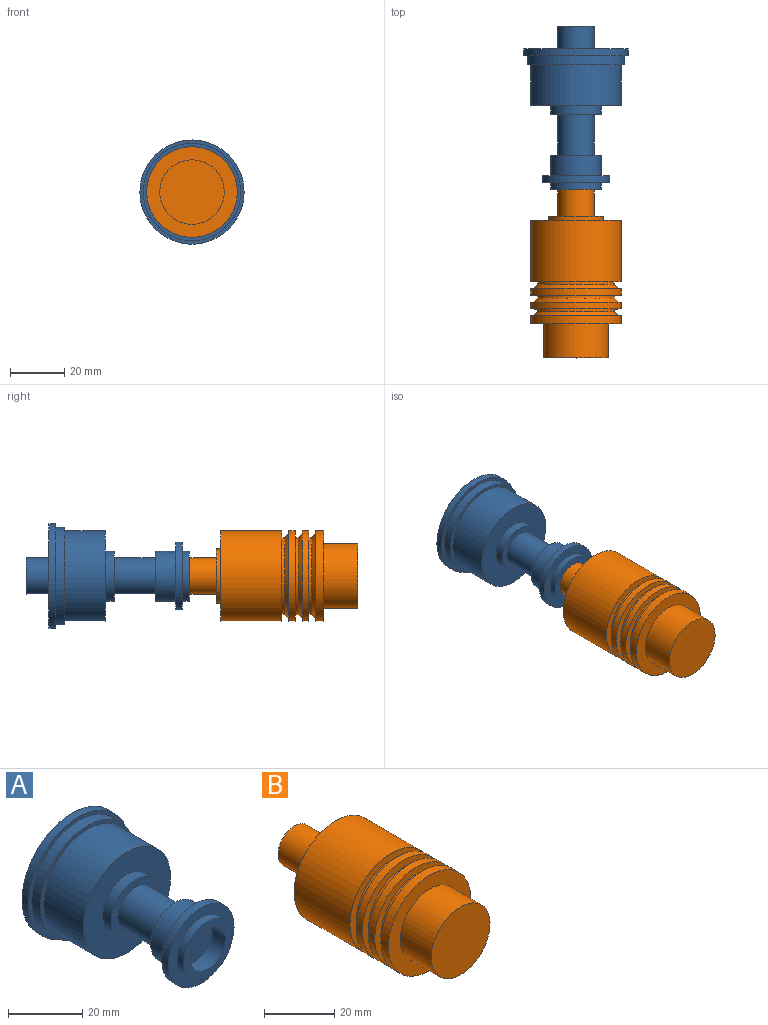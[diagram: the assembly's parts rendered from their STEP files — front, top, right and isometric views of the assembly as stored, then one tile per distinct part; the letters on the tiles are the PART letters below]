
ASSEMBLY  parts=2 mates=1
PART A: 25 faces, bbox 38.3x60x38.3 mm
  f0: plane 18.4x18.4mm, normal (0,-1,0), area 127mm2, adj f20,f21
  f1: plane 13.4x13.4mm, normal (0,1,0), area 71.6mm2, adj f2,f24
  f2: cylinder r=6.7mm len=13.4mm, axis (0,1,0), area 564.1mm2, adj f1,f3
  f3: plane 18.4x18.4mm, normal (0,1,0), area 124.9mm2, adj f2,f4
  f4: cylinder r=9.2mm len=18.4mm, axis (0,1,0), area 289mm2, adj f3,f5
  f5: plane 38.3x38.3mm, normal (0,1,0), area 886.2mm2, adj f4,f6
  f6: cylinder r=19.15mm len=38.3mm, axis (0,1,0), area 300.8mm2, adj f5,f7
  f7: plane 38.3x38.3mm, normal (0,-1,0), area 145.5mm2, adj f6,f8
  f8: cylinder r=17.9mm len=35.8mm, axis (0,1,0), area 371.1mm2, adj f7,f9
  f9: plane 35.8x35.8mm, normal (0,-1,0), area 135.7mm2, adj f8,f10
  f10: cylinder r=16.65mm len=33.3mm, axis (0,1,0), area 1569.2mm2, adj f9,f11
  f11: plane 33.3x33.3mm, normal (0,-1,0), area 605mm2, adj f10,f12
  f12: cylinder r=9.2mm len=18.4mm, axis (0,1,0), area 190.8mm2, adj f11,f13
  f13: plane 18.4x18.4mm, normal (0,-1,0), area 124.9mm2, adj f12,f14
  f14: cylinder r=6.7mm len=15mm, axis (0,1,0), area 631.5mm2, adj f13,f15
  f15: plane 18.4x18.4mm, normal (0,1,0), area 124.9mm2, adj f14,f16
  f16: cylinder r=9.2mm len=18.4mm, axis (0,1,0), area 433.5mm2, adj f15,f17
  f17: plane 25x25mm, normal (0,1,0), area 225mm2, adj f16,f18
  f18: cylinder r=12.5mm len=25mm, axis (0,1,0), area 196.3mm2, adj f17,f19
  f19: plane 25x25mm, normal (0,-1,0), area 225mm2, adj f18,f20
  f20: cylinder r=9.2mm len=18.4mm, axis (0,1,0), area 144.5mm2, adj f0,f19
  f21: cylinder r=6.65mm len=13.3mm, axis (0,-1,0), area 208.9mm2, adj f0,f22
  f22: plane 13.3x13.3mm, normal (0,-1,0), area 138.9mm2, adj f21
  f23: plane 9.4x9.4mm, normal (0,1,0), area 69.4mm2, adj f24
  f24: cylinder r=4.7mm len=10.9mm, axis (0,1,0), area 321.9mm2, adj f1,f23
PART B: 24 faces, bbox 33.3x67x33.3 mm
  f0: plane 33.3x33.3mm, normal (0,-1,0), area 429.8mm2, adj f14,f18
  f1: plane 33.3x33.3mm, normal (0,1,0), area 559.9mm2, adj f2,f20
  f2: cylinder r=16.65mm len=33.3mm, axis (0,1,0), area 2353.8mm2, adj f1,f3
  f3: plane 33.3x33.3mm, normal (0,-1,0), area 241.9mm2, adj f2,f4
  f4: cylinder r=14.15mm len=28.3mm, axis (0,1,0), area 88.9mm2, adj f3,f15
  f5: plane 33.3x33.3mm, normal (0,1,0), area 101.5mm2, adj f6,f15
  f6: cylinder r=16.65mm len=33.3mm, axis (0,1,0), area 261.5mm2, adj f5,f7
  f7: plane 33.3x33.3mm, normal (0,-1,0), area 241.9mm2, adj f6,f8
  f8: cylinder r=14.15mm len=28.3mm, axis (0,1,0), area 88.9mm2, adj f7,f16
  f9: plane 33.3x33.3mm, normal (0,1,0), area 101.5mm2, adj f10,f16
  f10: cylinder r=16.65mm len=33.3mm, axis (0,1,0), area 261.5mm2, adj f9,f11
  f11: plane 33.3x33.3mm, normal (0,-1,0), area 241.9mm2, adj f10,f12
  f12: cylinder r=14.15mm len=28.3mm, axis (0,1,0), area 88.9mm2, adj f11,f17
  f13: plane 33.3x33.3mm, normal (0,1,0), area 101.5mm2, adj f14,f17
  f14: cylinder r=16.65mm len=33.3mm, axis (0,1,0), area 313.8mm2, adj f0,f13
  f15: cone r=14.15mm half-angle=45deg, axis (0,-1,0), area 198.6mm2, adj f4,f5
  f16: cone r=14.15mm half-angle=45deg, axis (0,-1,0), area 198.6mm2, adj f8,f9
  f17: cone r=14.15mm half-angle=45deg, axis (0,-1,0), area 198.6mm2, adj f12,f13
  f18: cylinder r=11.85mm len=23.7mm, axis (0,1,0), area 930.7mm2, adj f0,f19
  f19: plane 23.7x23.7mm, normal (0,-1,0), area 441.2mm2, adj f18
  f20: cylinder r=9.95mm len=19.9mm, axis (0,-1,0), area 93.8mm2, adj f1,f21
  f21: plane 19.9x19.9mm, normal (0,1,0), area 172.1mm2, adj f20,f22
  f22: cylinder r=6.65mm len=15mm, axis (0,-1,0), area 626.7mm2, adj f21,f23
  f23: plane 13.3x13.3mm, normal (0,1,0), area 138.9mm2, adj f22
PLACE A t=(-3.3,41.13,-21.5)mm
PLACE B t=(-3.3,-19.37,-21.5)mm
MATE fastened A.f21 <-> B.f22  axis (0,-1,0) through (-3.3,16.13,-21.5)mm
